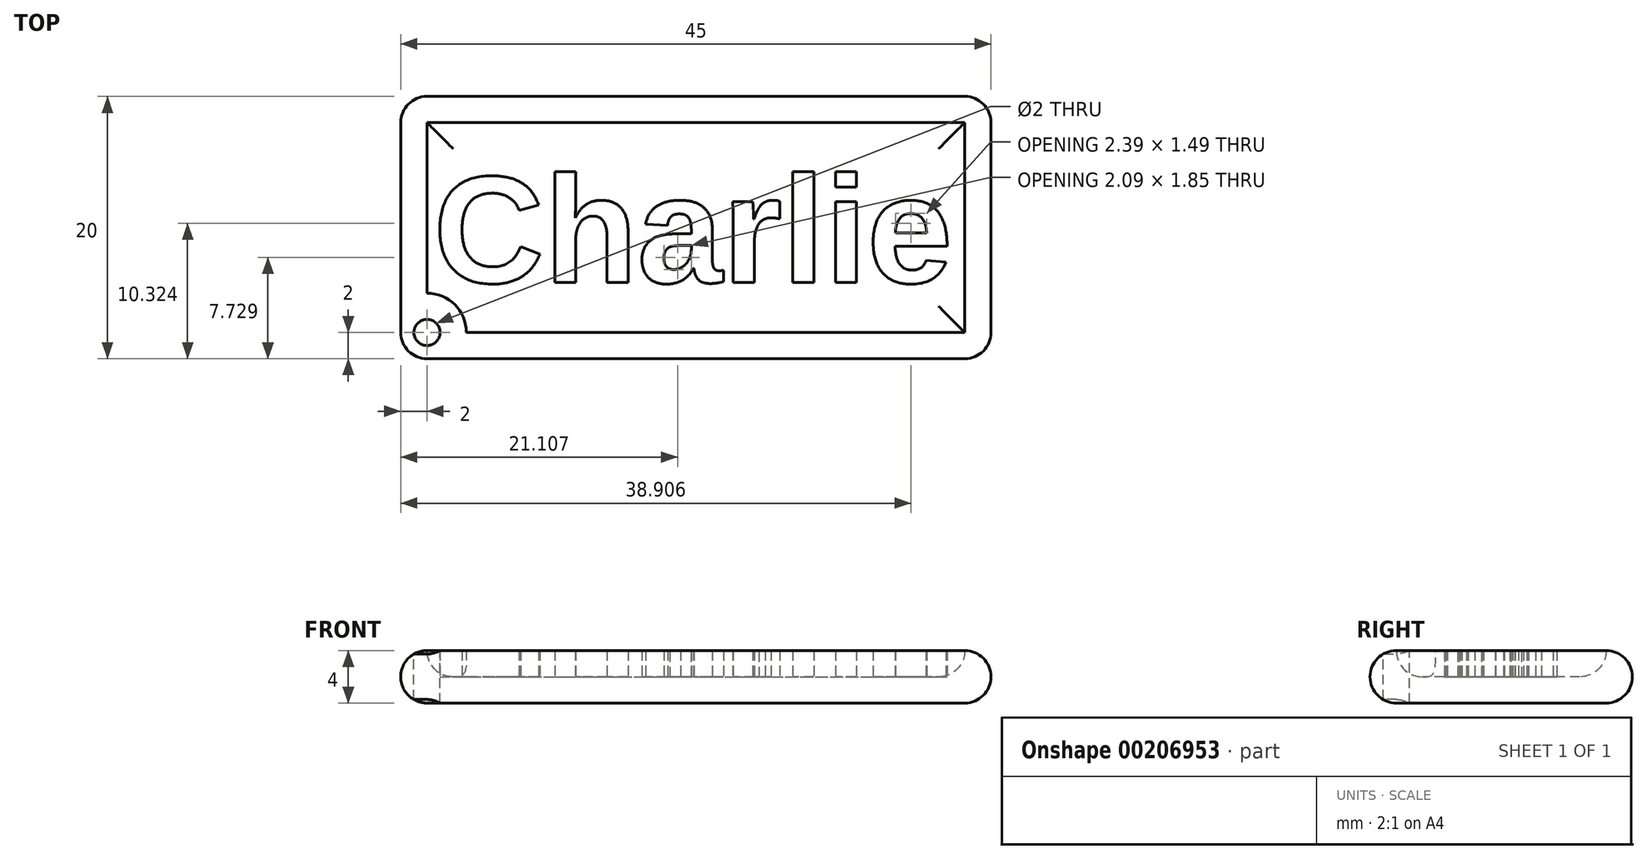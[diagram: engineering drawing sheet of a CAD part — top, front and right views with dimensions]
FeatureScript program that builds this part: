
annotation { "Feature Type Name" : "Feature", "Feature Type Description" : "" }
export const myFeature = defineFeature(function(context is Context, id is Id, definition is map)
    precondition{}
    {
        {
            var Q0;
            Q0=qCreatedBy(makeId("Top.planeOp"),FACE);
            var sketch = newSketch(context, id + "F0", { "sketchPlane" : qUnion([Q0])});
            skText(sketch, "E0", { "text": "Charlie", "fontName": "Arimo-Bold.ttf"});
            skLineSegment(sketch, "E1", {"start": v(-60, 4.97) * mm, "end": v(-20, 4.97) * mm, "construction": true});
            skPoint(sketch, "E2", {"position": v(-20, 4.97) * mm});
            skPoint(sketch, "E3.orphan", {"position": v(-40, 4.97) * mm});
            skLineSegment(sketch, "E4", {"start": v(20, 0) * mm, "end": v(-20, 0) * mm, "construction": true});
            skPoint(sketch, "E5", {"position": v(0, 0) * mm});
            const initialGuessF0  = {"E0": [-0.02, -0.0042, 1, 0, 0.0084]};
            skSetInitialGuess(sketch, initialGuessF0);
            skSolve(sketch);
        }
        {
            var Q0;
            Q0 = qSketchRegion(id + "F0", true);
            extrude(context, id + "F1", {"entities" : qUnion([Q0]), "depth" : 2 * mm});
        }
        {
            var Q0;
            Q0=qCreatedBy(makeId("Top.planeOp"),FACE);
            var sketch = newSketch(context, id + "F2", { "sketchPlane" : qUnion([Q0])});
            skLineSegment(sketch, "E6.bottom", {"start": v(-20.5, 10) * mm, "end": v(20.5, 10) * mm});
            skLineSegment(sketch, "E6.top", {"start": v(-20.5, -10) * mm, "end": v(20.5, -10) * mm});
            skLineSegment(sketch, "E6.left", {"start": v(-22.5, 8) * mm, "end": v(-22.5, -8) * mm});
            skLineSegment(sketch, "E6.right", {"start": v(22.5, 8) * mm, "end": v(22.5, -8) * mm});
            skPoint(sketch, "E7.visualSharp", {"position": v(-22.5, 10) * mm});
            skArc(sketch, "E7.filletArc", {"start": v(-20.5, 10) * mm, "mid": v(-21.91, 9.41) * mm, "end": v(-22.5, 8) * mm});
            skPoint(sketch, "E8.visualSharp", {"position": v(22.5, 10) * mm});
            skArc(sketch, "E8.filletArc", {"start": v(22.5, 8) * mm, "mid": v(21.91, 9.41) * mm, "end": v(20.5, 10) * mm});
            skPoint(sketch, "E9.visualSharp", {"position": v(22.5, -10) * mm});
            skArc(sketch, "E9.filletArc", {"start": v(20.5, -10) * mm, "mid": v(21.91, -9.41) * mm, "end": v(22.5, -8) * mm});
            skPoint(sketch, "E10.visualSharp", {"position": v(-22.5, -10) * mm});
            skArc(sketch, "E10.filletArc", {"start": v(-22.5, -8) * mm, "mid": v(-21.91, -9.41) * mm, "end": v(-20.5, -10) * mm});
            skCircle(sketch, "E11", {"center": v(-20.5, -8) * mm, "radius": 1 * mm});
            skLineSegment(sketch, "E12", {"start": v(0, 10) * mm, "end": v(0, -10) * mm, "construction": true});
            skLineSegment(sketch, "E13", {"start": v(-22.5, 0) * mm, "end": v(22.5, 0) * mm, "construction": true});
            skPoint(sketch, "E14", {"position": v(0, 0) * mm});
            skLineSegment(sketch, "E15", {"start": v(-20.5, -8) * mm, "end": v(-22.5, -8) * mm, "construction": true});
            skLineSegment(sketch, "E16", {"start": v(-20.5, -8) * mm, "end": v(-20.5, -10) * mm, "construction": true});
            skSolve(sketch);
        }
        {
            var Q0;
            Q0 = qSketchRegion(id + "F2", true);
            extrude(context, id + "F3", {"entities" : qUnion([Q0]), "oppositeDirection" : true, "depth" : 2 * mm, "hasSecondDirection" : true, "secondDirectionOppositeDirection" : false, "secondDirectionDepth" : 2 * mm});
        }
        {
            var Q0;
            Q0=makeQuery(id+"F3.opExtrude","CAP_FACE",FACE,{"disambiguationData":[OSD([sQuery(id+"F2.wireOp",EDGE,"E6.bottom"),sQuery(id+"F2.wireOp",EDGE,"E6.top"),sQuery(id+"F2.wireOp",EDGE,"E6.left"),sQuery(id+"F2.wireOp",EDGE,"E6.right"),sQuery(id+"F2.wireOp",EDGE,"E7.filletArc"),sQuery(id+"F2.wireOp",EDGE,"E8.filletArc"),sQuery(id+"F2.wireOp",EDGE,"E9.filletArc"),sQuery(id+"F2.wireOp",EDGE,"E10.filletArc"),sQuery(id+"F2.wireOp",EDGE,"E11")])],"isStart":true});
            shell(context, id + "F4", {"entities" : qUnion([Q0]), "thickness" : 2 * mm});
        }
        {
            var Q0;
            Q0=makeQuery(id+"F3.opExtrude","CAP_EDGE",EDGE,{"disambiguationData":[OSD([sQuery(id+"F2.wireOp",EDGE,"E9.filletArc")])],"isStart":true});
            var Q1;
            Q1=makeQuery(id+"F3.opExtrude","CAP_EDGE",EDGE,{"disambiguationData":[OSD([sQuery(id+"F2.wireOp",EDGE,"E6.top")])],"isStart":true});
            var Q2;
            Q2=makeQuery(id+"F3.opExtrude","CAP_EDGE",EDGE,{"disambiguationData":[OSD([sQuery(id+"F2.wireOp",EDGE,"E6.right")])],"isStart":true});
            var Q3;
            Q3=makeQuery(id+"F3.opExtrude","CAP_EDGE",EDGE,{"disambiguationData":[OSD([sQuery(id+"F2.wireOp",EDGE,"E8.filletArc")])],"isStart":true});
            var Q4;
            Q4=makeQuery(id+"F3.opExtrude","CAP_EDGE",EDGE,{"disambiguationData":[OSD([sQuery(id+"F2.wireOp",EDGE,"E6.bottom")])],"isStart":true});
            var Q5;
            Q5=makeQuery(id+"F3.opExtrude","CAP_EDGE",EDGE,{"disambiguationData":[OSD([sQuery(id+"F2.wireOp",EDGE,"E6.left")])],"isStart":true});
            var Q6;
            Q6=makeQuery(id+"F3.opExtrude","CAP_EDGE",EDGE,{"disambiguationData":[OSD([sQuery(id+"F2.wireOp",EDGE,"E7.filletArc")])],"isStart":true});
            var Q7;
            Q7=makeQuery(id+"F3.opExtrude","CAP_EDGE",EDGE,{"disambiguationData":[OSD([sQuery(id+"F2.wireOp",EDGE,"E10.filletArc")])],"isStart":true});
            var Q8;
            Q8=makeQuery(id+"F3.opExtrude","CAP_EDGE",EDGE,{"disambiguationData":[OSD([sQuery(id+"F2.wireOp",EDGE,"E10.filletArc")])],"isStart":false});
            var Q9;
            Q9=makeQuery(id+"F3.opExtrude","CAP_EDGE",EDGE,{"disambiguationData":[OSD([sQuery(id+"F2.wireOp",EDGE,"E6.top")])],"isStart":false});
            var Q10;
            Q10=makeQuery(id+"F3.opExtrude","CAP_EDGE",EDGE,{"disambiguationData":[OSD([sQuery(id+"F2.wireOp",EDGE,"E6.left")])],"isStart":false});
            var Q11;
            Q11=makeQuery(id+"F3.opExtrude","CAP_EDGE",EDGE,{"disambiguationData":[OSD([sQuery(id+"F2.wireOp",EDGE,"E7.filletArc")])],"isStart":false});
            var Q12;
            Q12=makeQuery(id+"F3.opExtrude","CAP_EDGE",EDGE,{"disambiguationData":[OSD([sQuery(id+"F2.wireOp",EDGE,"E6.bottom")])],"isStart":false});
            var Q13;
            Q13=makeQuery(id+"F3.opExtrude","CAP_EDGE",EDGE,{"disambiguationData":[OSD([sQuery(id+"F2.wireOp",EDGE,"E9.filletArc")])],"isStart":false});
            var Q14;
            Q14=makeQuery(id+"F3.opExtrude","CAP_EDGE",EDGE,{"disambiguationData":[OSD([sQuery(id+"F2.wireOp",EDGE,"E6.right")])],"isStart":false});
            var Q15;
            Q15=makeQuery(id+"F3.opExtrude","CAP_EDGE",EDGE,{"disambiguationData":[OSD([sQuery(id+"F2.wireOp",EDGE,"E8.filletArc")])],"isStart":false});
            fillet(context, id + "F5", {"entities" : qUnion([Q0, Q1, Q2, Q3, Q4, Q5, Q6, Q7, Q8, Q9, Q10, Q11, Q12, Q13, Q14, Q15]), "radius" : 2 * mm, "tangentPropagation" : true, "allowEdgeOverflow" : false});
        }
        {
            var Q0;
            {var subQ0=sQuery(id+"F2.wireOp",EDGE,"E6.bottom");Q0=makeQuery(id+"F4.opShell","OFFSET_EDGE",EDGE,{"disambiguationData":[OSD([subQ0]),TDD([makeQuery(id+"F3.opExtrude","CAP_EDGE",EDGE,{"disambiguationData":[OSD([subQ0])],"isStart":false})])]});}
            var Q1;
            {var subQ0=sQuery(id+"F2.wireOp",EDGE,"E6.right");Q1=makeQuery(id+"F4.opShell","OFFSET_EDGE",EDGE,{"disambiguationData":[OSD([subQ0]),TDD([makeQuery(id+"F3.opExtrude","CAP_EDGE",EDGE,{"disambiguationData":[OSD([subQ0])],"isStart":false})])]});}
            var Q2;
            {var subQ0=sQuery(id+"F2.wireOp",EDGE,"E6.left");Q2=makeQuery(id+"F4.opShell","OFFSET_EDGE",EDGE,{"disambiguationData":[OSD([subQ0]),TDD([makeQuery(id+"F3.opExtrude","CAP_EDGE",EDGE,{"disambiguationData":[OSD([subQ0])],"isStart":false})])]});}
            var Q3;
            {var subQ0=sQuery(id+"F2.wireOp",EDGE,"E6.top");Q3=makeQuery(id+"F4.opShell","OFFSET_EDGE",EDGE,{"disambiguationData":[OSD([subQ0]),TDD([makeQuery(id+"F3.opExtrude","CAP_EDGE",EDGE,{"disambiguationData":[OSD([subQ0])],"isStart":false})])]});}
            fillet(context, id + "F6", {"entities" : qUnion([Q0, Q1, Q2, Q3]), "radius" : 2 * mm, "tangentPropagation" : true, "allowEdgeOverflow" : false});
        }
    });
